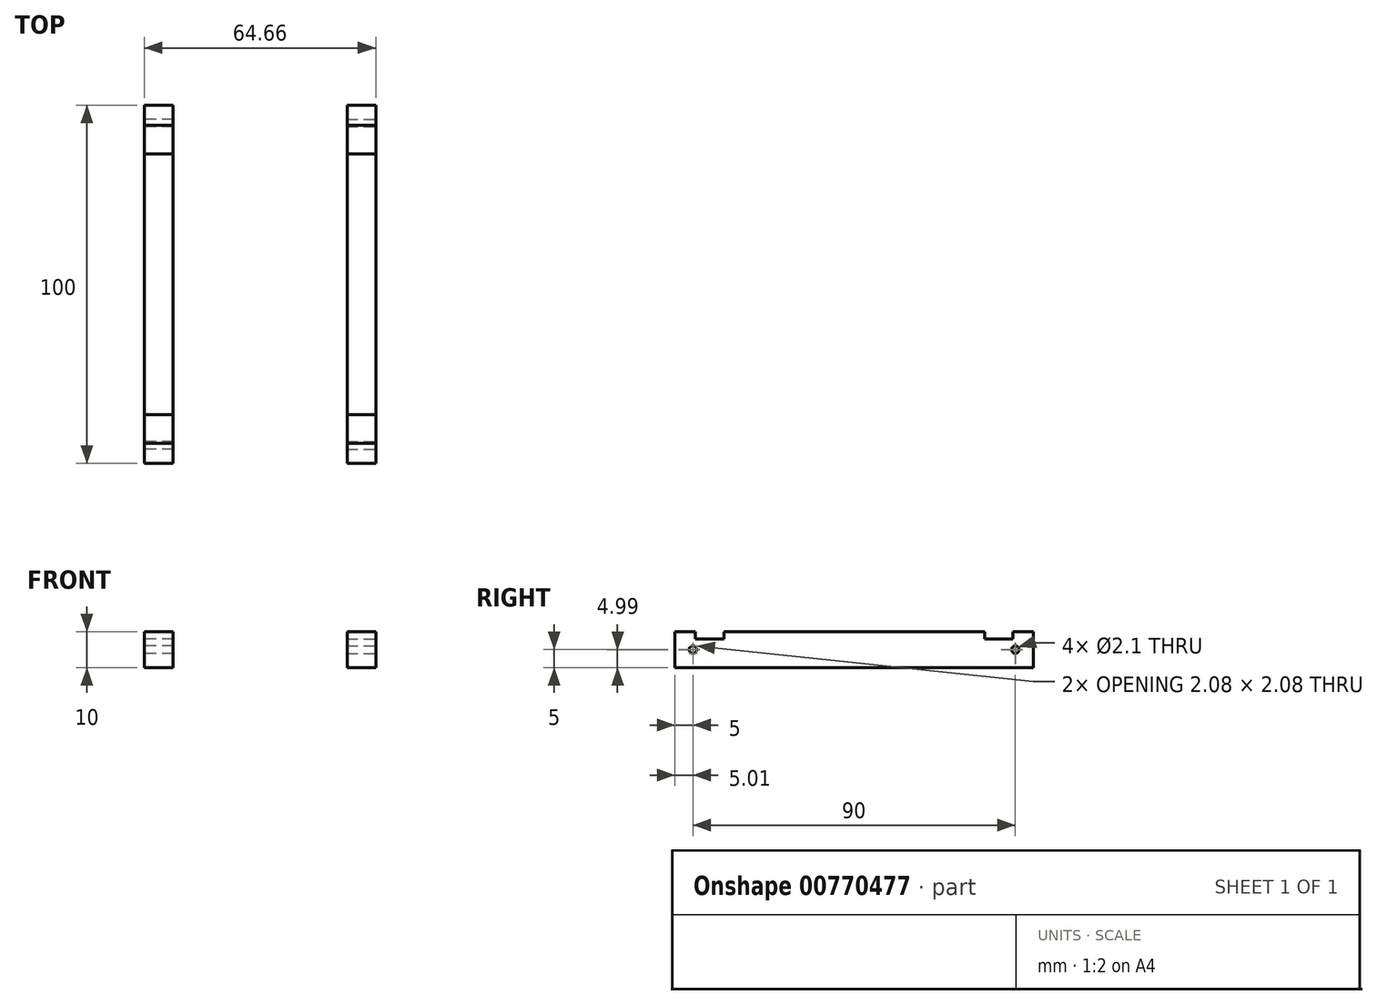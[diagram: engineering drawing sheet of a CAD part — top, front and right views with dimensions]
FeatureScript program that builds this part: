
annotation { "Feature Type Name" : "Feature", "Feature Type Description" : "" }
export const myFeature = defineFeature(function(context is Context, id is Id, definition is map)
    precondition{}
    {
        {
            var Q0;
            Q0=qCreatedBy(makeId("Top.planeOp"),FACE);
            var sketch = newSketch(context, id + "F0", { "sketchPlane" : qUnion([Q0])});
            skLineSegment(sketch, "E0.bottom", {"start": v(32.33, 50) * mm, "end": v(24.33, 50) * mm});
            skLineSegment(sketch, "E0.top", {"start": v(32.33, -50) * mm, "end": v(24.33, -50) * mm});
            skLineSegment(sketch, "E0.left", {"start": v(32.33, 50) * mm, "end": v(32.33, -50) * mm});
            skLineSegment(sketch, "E0.right", {"start": v(24.33, 50) * mm, "end": v(24.33, -50) * mm});
            skPoint(sketch, "E0.middle", {"position": v(28.33, 0) * mm});
            skLineSegment(sketch, "E1.MirrorCS", {"start": v(-24.33, 50) * mm, "end": v(-24.33, -50) * mm});
            skLineSegment(sketch, "E2.MirrorCS", {"start": v(-32.33, 50) * mm, "end": v(-32.33, -50) * mm});
            skLineSegment(sketch, "E3.MirrorCS", {"start": v(-32.33, 50) * mm, "end": v(-24.33, 50) * mm});
            skLineSegment(sketch, "E4.MirrorCS", {"start": v(-32.33, -50) * mm, "end": v(-24.33, -50) * mm});
            skPoint(sketch, "E5.MirrorP", {"position": v(-28.33, 0) * mm});
            skSolve(sketch);
        }
        {
            var Q0;
            Q0=makeQuery(id+"F0.imprint","IMPRINT",FACE,{"disambiguationData":[TD([[makeQuery(id+"F0.imprint","IMPRINT",EDGE,{"derivedFrom":sQuery(id+"F0.wireOp",EDGE,"E1.MirrorCS")}),-1.0]])]});
            var Q1;
            Q1=makeQuery(id+"F0.imprint","IMPRINT",FACE,{"disambiguationData":[TD([[makeQuery(id+"F0.imprint","IMPRINT",EDGE,{"derivedFrom":sQuery(id+"F0.wireOp",EDGE,"E0.bottom")}),1.0]])]});
            extrude(context, id + "F1", {"entities" : qUnion([Q0, Q1]), "depth" : 10 * mm, "offsetDistance" : 25 * mm});
        }
        {
            var Q0;
            Q0=makeQuery(id+"F1.opExtrude","SWEPT_FACE",FACE,{"disambiguationData":[OSD([sQuery(id+"F0.wireOp",EDGE,"E0.left")])]});
            var sketch = newSketch(context, id + "F2", { "sketchPlane" : qUnion([Q0])});
            skCircle(sketch, "E6", {"center": v(45, 5) * mm, "radius": 1.05 * mm});
            skCircle(sketch, "E7.MirrorC", {"center": v(-45, 5) * mm, "radius": 1.05 * mm});
            skLineSegment(sketch, "E8.bottom", {"start": v(44.38, 12) * mm, "end": v(36.38, 12) * mm});
            skLineSegment(sketch, "E8.top", {"start": v(44.38, 8) * mm, "end": v(36.38, 8) * mm});
            skLineSegment(sketch, "E8.left", {"start": v(44.38, 12) * mm, "end": v(44.38, 8) * mm});
            skLineSegment(sketch, "E8.right", {"start": v(36.38, 12) * mm, "end": v(36.38, 8) * mm});
            skPoint(sketch, "E8.middle", {"position": v(40.38, 10) * mm});
            skPoint(sketch, "E9.MirrorP", {"position": v(-40.38, 10) * mm});
            skLineSegment(sketch, "E10.MirrorCS", {"start": v(-36.38, 12) * mm, "end": v(-36.38, 8) * mm});
            skLineSegment(sketch, "E11.MirrorCS", {"start": v(-44.38, 12) * mm, "end": v(-36.38, 12) * mm});
            skLineSegment(sketch, "E12.MirrorCS", {"start": v(-44.38, 8) * mm, "end": v(-36.38, 8) * mm});
            skLineSegment(sketch, "E13.MirrorCS", {"start": v(-44.38, 12) * mm, "end": v(-44.38, 8) * mm});
            skSolve(sketch);
        }
        {
            var Q0;
            Q0 = qSketchRegion(id + "F2", true);
            extrude(context, id + "F3", {"entities" : qUnion([Q0]), "operationType" : NewBodyOperationType.REMOVE, "endBound" : BoundingType.THROUGH_ALL, "oppositeDirection" : true, "depth" : 25 * mm, "offsetDistance" : 25 * mm});
        }
        {
            var Q0;
            Q0=makeQuery(id+"F1.opExtrude","SWEPT_BODY",BODY,{"disambiguationData":[OSD([sQuery(id+"F0.wireOp",EDGE,"E1.MirrorCS"),sQuery(id+"F0.wireOp",EDGE,"E2.MirrorCS"),sQuery(id+"F0.wireOp",EDGE,"E3.MirrorCS"),sQuery(id+"F0.wireOp",EDGE,"E4.MirrorCS")])]});
            deleteBodies(context, id + "F4", {"entities" : qUnion([Q0])});
        }
        {
            var Q0;
            Q0=makeQuery(id+"F1.opExtrude","SWEPT_BODY",BODY,{"disambiguationData":[OSD([sQuery(id+"F0.wireOp",EDGE,"E0.bottom"),sQuery(id+"F0.wireOp",EDGE,"E0.top"),sQuery(id+"F0.wireOp",EDGE,"E0.left"),sQuery(id+"F0.wireOp",EDGE,"E0.right")])]});
            var Q1;
            Q1=qCreatedBy(makeId("Right.planeOp"),FACE);
            mirror(context, id + "F5", {"entities" : qUnion([Q0]), "mirrorPlane" : qUnion([Q1])});
        }
    });
